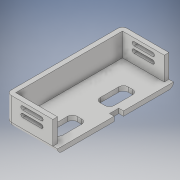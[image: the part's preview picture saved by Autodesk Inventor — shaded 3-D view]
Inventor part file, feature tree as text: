
AUTODESK INVENTOR PART (.ipt)
format: ipt  version: 2019.4 (Build 234330000, 330)  size: 200,704 bytes
history: native  units: mm
features: extrude x5, sketch x5, fillet x2, pattern_linear x1
ambient origin geometry x8: Origin, YZ Plane, XZ Plane, XY Plane, X Axis, Y Axis, Z Axis, Center Point
bodies: Solid1 (feature_tree)
feature tree (13):
  extrude  "Extrusion1"  Depth=115.0mm
  extrude  "Extrusion2"  Depth=5.0mm TaperAngle=0.0deg
  extrude  "Extrusion3"  Depth=115.0mm
  extrude  "Extrusion4"  Depth=25.0mm TaperAngle=0.0deg
  fillet  "Fillet1"  Radius=5.5mm
  fillet  "Fillet2"  Radius=10.0mm
  pattern_linear  "Rectangular Pattern1"  Spacing1=4.0mm  [1 undecoded]
  extrude  "Extrusion5"  Depth=125.0mm TaperAngle=0.0deg
  sketch  "Sketch1"  dims[d0=45.0mm d1=115.0mm]
  sketch  "Sketch2"  dims[d2=5.0mm d3=5.0mm d4=0.0mm]
  sketch  "Sketch3"  dims[d5=45.0mm d6=115.0mm]
  sketch  "Sketch4"  dims[d7=5.0mm d8=25.0mm d9=0.0mm d10=5.5mm d11=10.0mm]
  sketch  "Sketch5"  dims[d12=0.0mm d13=4.0mm d14=125.0mm d15=0.0mm d16=25.0mm d17=6.0mm d18=15.0mm d19=30.0mm d20=20.0mm d22=55.0mm d23=10.0mm d25=10.0mm d27=5.0mm d28=0.0mm d29=5.0mm d30=5.0mm d31=20.0mm d33=7.0mm d34=5.0mm d35=5.0mm d36=5.0mm d37=0.0mm]
note: 1 required parameter value undecoded (feature->parameter linkage not recoverable at this tier; creation-order binding heuristic only, values carry confidence <= 0.55)
